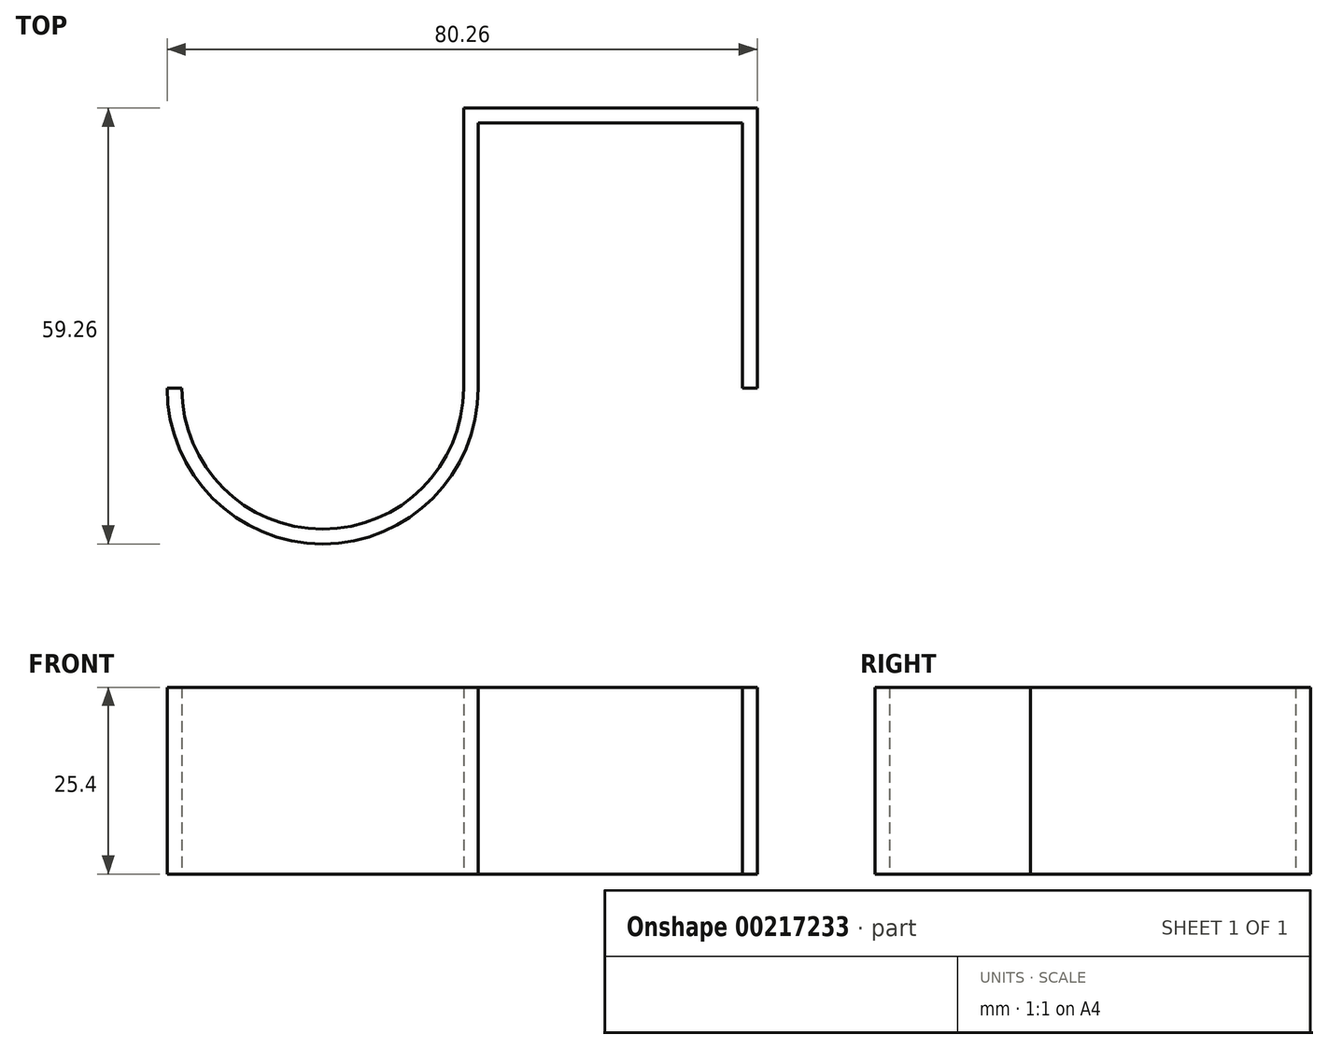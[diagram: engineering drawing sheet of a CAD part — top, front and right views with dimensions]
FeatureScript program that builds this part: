
annotation { "Feature Type Name" : "Feature", "Feature Type Description" : "" }
export const myFeature = defineFeature(function(context is Context, id is Id, definition is map)
    precondition{}
    {
        {
            var Q0;
            Q0=qCreatedBy(makeId("Top.planeOp"),FACE);
            var sketch = newSketch(context, id + "F0", { "sketchPlane" : qUnion([Q0])});
            skLineSegment(sketch, "E0", {"start": v(0, 0) * mm, "end": v(0, 38.1) * mm});
            skLineSegment(sketch, "E1", {"start": v(0, 38.1) * mm, "end": v(-39.94, 38.1) * mm});
            skLineSegment(sketch, "E2", {"start": v(-39.94, 38.1) * mm, "end": v(-39.94, 0) * mm});
            skArc(sketch, "E3", {"start": v(-78.26, 0) * mm, "mid": v(-59.1, -19.16) * mm, "end": v(-39.94, 0) * mm});
            skLineSegment(sketch, "E4", {"start": v(-78.26, 0) * mm, "end": v(-80.26, 0) * mm});
            skArc(sketch, "E5", {"start": v(-80.26, 0) * mm, "mid": v(-59.1, -21.16) * mm, "end": v(-37.94, 0) * mm});
            skLineSegment(sketch, "E6", {"start": v(-37.94, 0) * mm, "end": v(-37.94, 36.1) * mm});
            skLineSegment(sketch, "E7", {"start": v(-37.94, 36.1) * mm, "end": v(-2, 36.1) * mm});
            skLineSegment(sketch, "E8", {"start": v(-2, 36.1) * mm, "end": v(-2, 0) * mm});
            skLineSegment(sketch, "E9", {"start": v(-2, 0) * mm, "end": v(0, 0) * mm});
            skSolve(sketch);
        }
        {
            var Q0;
            Q0 = qSketchRegion(id + "F0", true);
            extrude(context, id + "F1", {"entities" : qUnion([Q0]), "depth" : 25.4 * mm});
        }
    });
